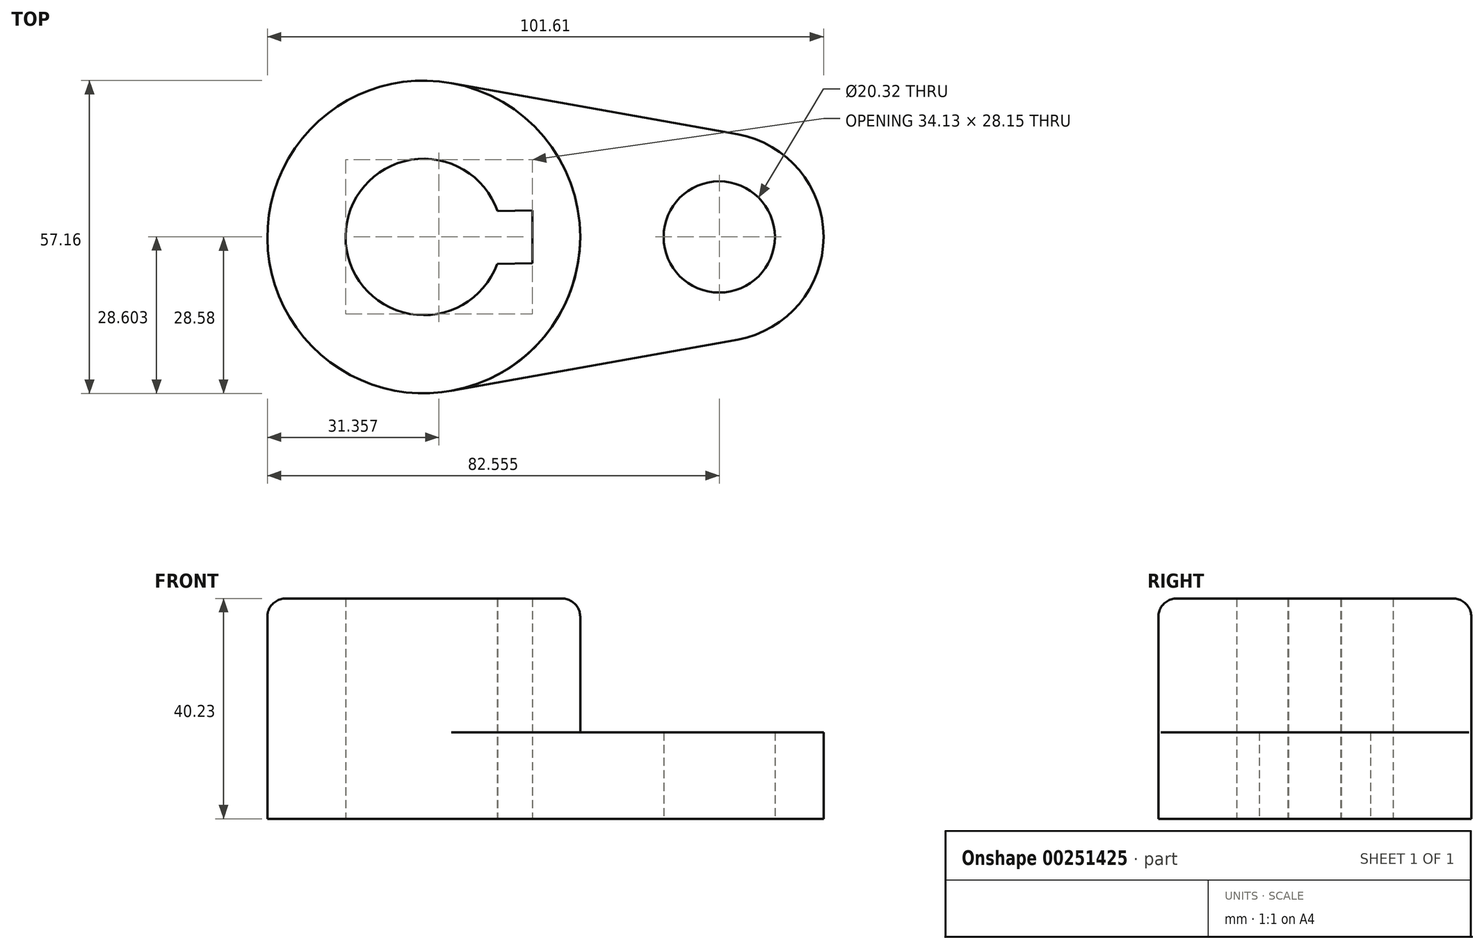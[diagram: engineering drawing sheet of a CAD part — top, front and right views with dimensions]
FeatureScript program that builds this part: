
annotation { "Feature Type Name" : "Feature", "Feature Type Description" : "" }
export const myFeature = defineFeature(function(context is Context, id is Id, definition is map)
    precondition{}
    {
        {
            var Q0;
            Q0=qCreatedBy(makeId("Top.planeOp"),FACE);
            var sketch = newSketch(context, id + "F0", { "sketchPlane" : qUnion([Q0])});
            skArc(sketch, "E0", {"start": v(13.5, 4.7) * mm, "mid": v(-14.29, 0.13) * mm, "end": v(13.4, -4.95) * mm});
            skCircle(sketch, "E1", {"center": v(53.98, 0) * mm, "radius": 10.16 * mm});
            skCircle(sketch, "E2", {"center": v(0, 0) * mm, "radius": 28.58 * mm});
            skCircle(sketch, "E3", {"center": v(53.98, 0) * mm, "radius": 19.05 * mm});
            skPoint(sketch, "E4.visualSharp", {"position": v(33.04, -28.58) * mm});
            skLineSegment(sketch, "E5.right", {"start": v(19.84, -4.83) * mm, "end": v(19.84, 4.83) * mm});
            skLineSegment(sketch, "E6.trimOffspring", {"start": v(13.5, 4.7) * mm, "end": v(19.84, 4.83) * mm});
            skLineSegment(sketch, "E7.trimOffspring", {"start": v(13.4, -4.95) * mm, "end": v(19.84, -4.83) * mm});
            skLineSegment(sketch, "E8", {"start": v(5.04, 28.13) * mm, "end": v(57.34, 18.75) * mm});
            skLineSegment(sketch, "E9", {"start": v(5.04, -28.13) * mm, "end": v(57.34, -18.75) * mm});
            skLineSegment(sketch, "E10", {"start": v(0, 0) * mm, "end": v(61.19, 0) * mm, "construction": true});
            skPoint(sketch, "E11.endSnap0", {"position": v(-14.29, 0.13) * mm});
            skPoint(sketch, "E12.endSnap0", {"position": v(19.84, 0) * mm});
            skSolve(sketch);
        }
        {
            var Q0;
            Q0=makeQuery(id+"F0.imprint","IMPRINT",FACE,{"disambiguationData":[TD([[makeQuery(id+"F0.imprint","IMPRINT",EDGE,{"derivedFrom":sQuery(id+"F0.wireOp",EDGE,"E0")}),-1.0]])]});
            extrude(context, id + "F1", {"entities" : qUnion([Q0]), "depth" : 40.23 * mm});
        }
        {
            var Q0;
            {var subQ0=sQuery(id+"F0.wireOp",EDGE,"o5OdITKO-bEnJ-2VYi-a7Jk-zIUuU5JH3HSI");var subQ1=sQuery(id+"F0.wireOp",EDGE,"E2");var subQ2=makeQuery(id+"F0.imprint","INTERSECT",VERTEX,{"disambiguationData":[OD(1.0)],"derivedFrom":[subQ1,subQ0]});Q0=makeQuery(id+"F0.imprint","IMPRINT",FACE,{"disambiguationData":[TD([[makeQuery(id+"F0.imprint","IMPRINT",EDGE,{"disambiguationData":[TD([[subQ2,1.0]])],"derivedFrom":subQ1}),-1.0]])]});}
            var Q1;
            Q1=makeQuery(id+"F0.imprint","IMPRINT",FACE,{"disambiguationData":[TD([[makeQuery(id+"F0.imprint","IMPRINT",EDGE,{"derivedFrom":sQuery(id+"F0.wireOp",EDGE,"E1")}),-1.0]])]});
            extrude(context, id + "F2", {"entities" : qUnion([Q0, Q1]), "operationType" : NewBodyOperationType.ADD, "depth" : 15.77 * mm});
        }
        {
            var Q0;
            {var subQ0=sQuery(id+"F0.wireOp",EDGE,"E2");Q0=makeQuery(id+"F1.opExtrude","CAP_EDGE",EDGE,{"disambiguationData":[OSD([subQ0]),TDD([makeQuery(id+"F0.imprint","IMPRINT",EDGE,{"disambiguationData":[TD([[makeQuery(id+"F0.imprint","INTERSECT",VERTEX,{"disambiguationData":[OD(0.0)],"derivedFrom":[subQ0,sQuery(id+"F0.wireOp",EDGE,"SRnHb5uK-vhAm-8B8o-SrwD-EHZrL22LgCVp")]}),1.0]])],"derivedFrom":subQ0})])],"isStart":false});}
            var Q1;
            Q1=makeQuery(id+"F1.opExtrude","CAP_EDGE",EDGE,{"disambiguationData":[OSD([sQuery(id+"F0.wireOp",EDGE,"SRnHb5uK-vhAm-8B8o-SrwD-EHZrL22LgCVp")])],"isStart":false});
            var Q2;
            {var subQ0=sQuery(id+"F0.wireOp",EDGE,"E2");Q2=makeQuery(id+"F1.opExtrude","CAP_EDGE",EDGE,{"disambiguationData":[OSD([subQ0]),TDD([makeQuery(id+"F0.imprint","IMPRINT",EDGE,{"disambiguationData":[TD([[makeQuery(id+"F0.imprint","INTERSECT",VERTEX,{"disambiguationData":[OD(1.0)],"derivedFrom":[subQ0,sQuery(id+"F0.wireOp",EDGE,"o5OdITKO-bEnJ-2VYi-a7Jk-zIUuU5JH3HSI")]}),1.0]])],"derivedFrom":subQ0})])],"isStart":false});}
            var Q3;
            Q3=makeQuery(id+"F1.opExtrude","CAP_EDGE",EDGE,{"disambiguationData":[OSD([sQuery(id+"F0.wireOp",EDGE,"o5OdITKO-bEnJ-2VYi-a7Jk-zIUuU5JH3HSI")])],"isStart":false});
            fillet(context, id + "F3", {"entities" : qUnion([Q0, Q1, Q2, Q3]), "radius" : 3.3 * mm, "tangentPropagation" : true, "allowEdgeOverflow" : false});
        }
    });
